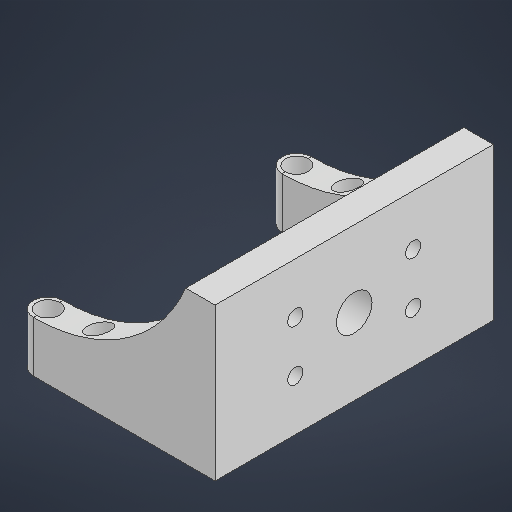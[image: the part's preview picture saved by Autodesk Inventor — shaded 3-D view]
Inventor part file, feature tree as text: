
AUTODESK INVENTOR PART (.ipt)
format: ipt  version: 2025.1 (Build 291241000, 241)  size: 602,112 bytes
history: native  units: in
note: dims shown in document units (in); Inventor stores cm internally (conversion verified against a paired STEP export)
features: extrude x7, sketch x6, projected_geometry x6, plane x1, mirror x1
ambient origin geometry x8: Origin, YZ Plane, XZ Plane, XY Plane, X Axis, Y Axis, Z Axis, Center Point
bodies: Solid1 (feature_tree)
feature tree (21):
  sketch  "Sketch1"  dims[d0=0.2283in d1=0.2283in d2=0.2283in d3=0.2283in d4=0.1772in d5=0.1772in]
  extrude  "Extrusion1"  Depth=0.1772in
  extrude  "Extrusion2"  Depth=0.1772in
  extrude  "Extrusion3"  Depth=0.7874in
  extrude  "Extrusion4"  Depth=0.3937in
  extrude  "Extrusion5"  Depth=0.3937in
  plane  "Work Plane1"
  mirror  "Mirror1"
  extrude  "Extrusion6"  Depth=0.3937in
  extrude  "Extrusion7"  Depth=0.3937in
  sketch  "Sketch2"  dims[d6=0.1772in d7=0.1772in]
  sketch  "Sketch3"  dims[d8=1.0157in d9=0.7874in]
  projected_geometry  "Projected Loop1"
  sketch  "Sketch4"  dims[d10=0.3937in d11=0.0in d12=0.7874in]
  projected_geometry  "Projected Loop2"
  projected_geometry  "Projected Loop3"
  sketch  "Sketch5"  dims[d13=0.3937in d14=0.0in d15=0.2165in]
  projected_geometry  "Projected Loop4"
  projected_geometry  "Projected Loop5"
  sketch  "Sketch6"  dims[d16=0.3937in d17=0.3937in d18=0.2165in d19=0.2165in d20=0.3937in d21=0.2165in d22=1.7008in d23=1.1811in d24=0.126in d25=0.0in d26=0.1181in d27=0.1181in d28=0.1181in d29=0.1181in d30=0.3937in d31=0.0in d32=0.2313in d33=0.0in d34=-0.8504in d35=1.3312in d36=0.0in d37=0.2756in d38=0.0in d39=0.0in]
  projected_geometry  "Projected Loop6"
